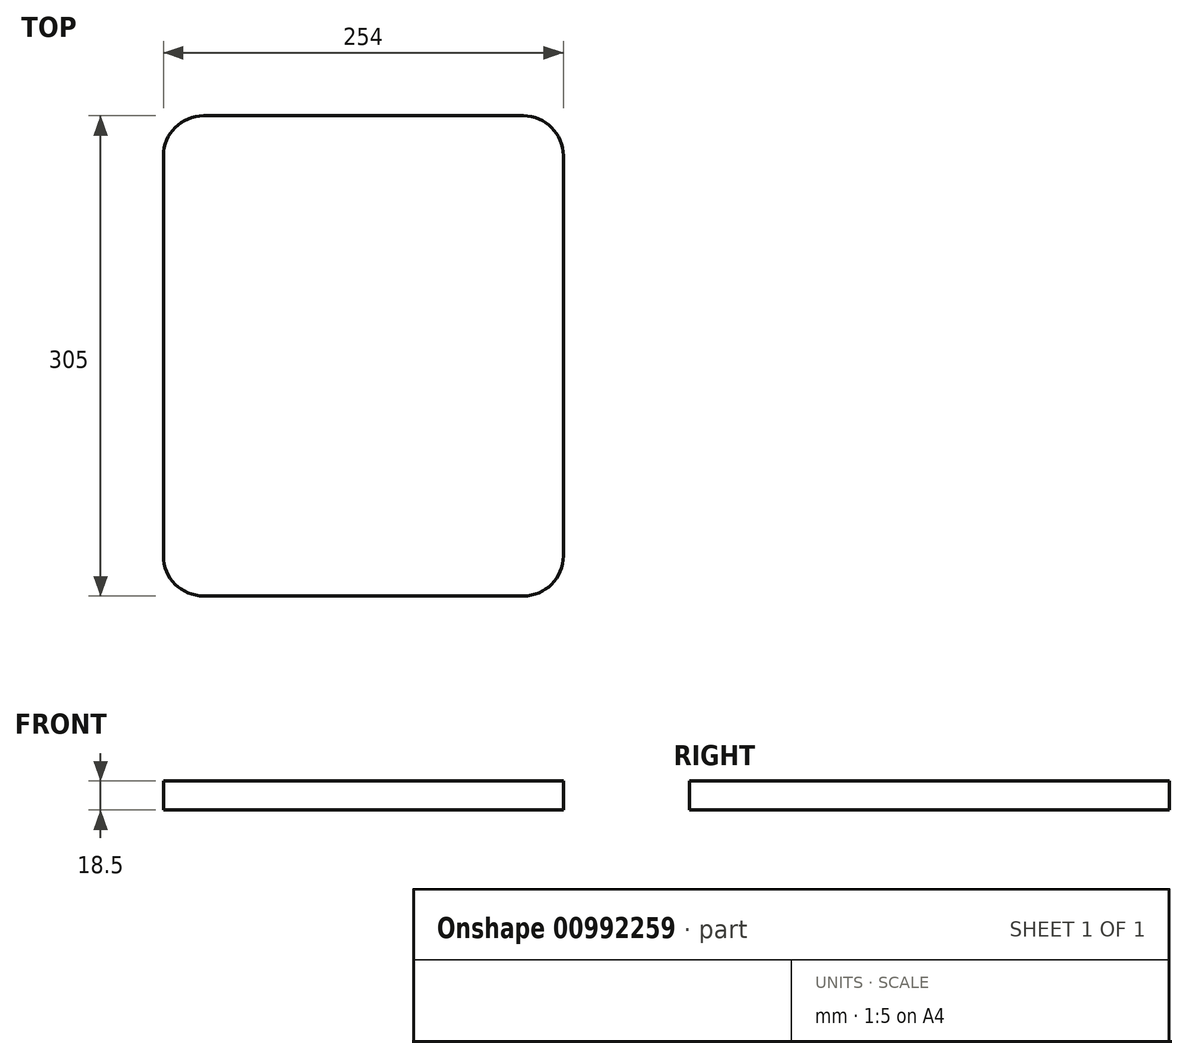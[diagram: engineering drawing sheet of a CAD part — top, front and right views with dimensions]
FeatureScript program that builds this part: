
annotation { "Feature Type Name" : "Feature", "Feature Type Description" : "" }
export const myFeature = defineFeature(function(context is Context, id is Id, definition is map)
    precondition{}
    {
        {
            var Q0;
            Q0=qCreatedBy(makeId("Top.planeOp"),FACE);
            var sketch = newSketch(context, id + "F0", { "sketchPlane" : qUnion([Q0])});
            skLineSegment(sketch, "E0.bottom", {"start": v(127, 152.5) * mm, "end": v(-127, 152.5) * mm});
            skLineSegment(sketch, "E0.top", {"start": v(127, -152.5) * mm, "end": v(-127, -152.5) * mm});
            skLineSegment(sketch, "E0.left", {"start": v(127, 152.5) * mm, "end": v(127, -152.5) * mm});
            skLineSegment(sketch, "E0.right", {"start": v(-127, 152.5) * mm, "end": v(-127, -152.5) * mm});
            skPoint(sketch, "E0.middle", {"position": v(0, 0) * mm});
            skSolve(sketch);
        }
        {
            var Q0;
            Q0=makeQuery(id+"F0.imprint","IMPRINT",FACE,{"disambiguationData":[TD([[makeQuery(id+"F0.imprint","IMPRINT",EDGE,{"derivedFrom":sQuery(id+"F0.wireOp",EDGE,"E0.bottom")}),1.0]])]});
            extrude(context, id + "F1", {"entities" : qUnion([Q0]), "depth" : 18.5 * mm, "offsetDistance" : 25 * mm});
        }
        {
            var Q0;
            Q0=makeQuery(id+"F1.opExtrude","SWEPT_EDGE",EDGE,{"disambiguationData":[OSD([sQuery(id+"F0.wireOp",EDGE,"E0.top"),sQuery(id+"F0.wireOp",EDGE,"E0.left")])]});
            var Q1;
            Q1=makeQuery(id+"F1.opExtrude","SWEPT_EDGE",EDGE,{"disambiguationData":[OSD([sQuery(id+"F0.wireOp",EDGE,"E0.top"),sQuery(id+"F0.wireOp",EDGE,"E0.right")])]});
            var Q2;
            Q2=makeQuery(id+"F1.opExtrude","SWEPT_EDGE",EDGE,{"disambiguationData":[OSD([sQuery(id+"F0.wireOp",EDGE,"E0.bottom"),sQuery(id+"F0.wireOp",EDGE,"E0.left")])]});
            var Q3;
            Q3=makeQuery(id+"F1.opExtrude","SWEPT_EDGE",EDGE,{"disambiguationData":[OSD([sQuery(id+"F0.wireOp",EDGE,"E0.bottom"),sQuery(id+"F0.wireOp",EDGE,"E0.right")])]});
            fillet(context, id + "F2", {"entities" : qUnion([Q0, Q1, Q2, Q3]), "radius" : 25.4 * mm, "tangentPropagation" : true, "allowEdgeOverflow" : false});
        }
    });
